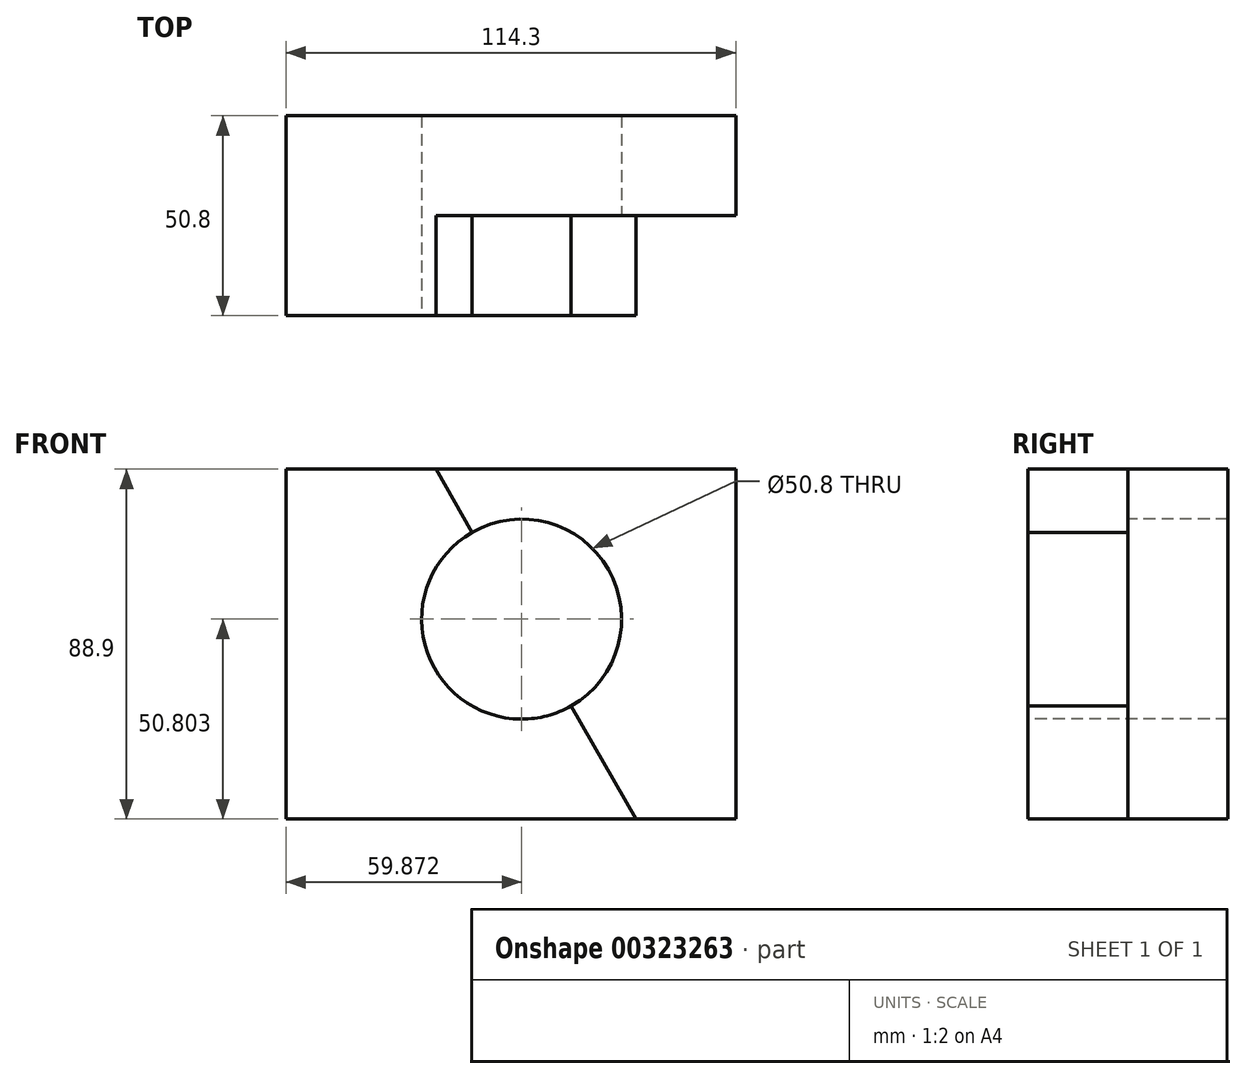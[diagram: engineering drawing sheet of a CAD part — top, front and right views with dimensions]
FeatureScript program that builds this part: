
annotation { "Feature Type Name" : "Feature", "Feature Type Description" : "" }
export const myFeature = defineFeature(function(context is Context, id is Id, definition is map)
    precondition{}
    {
        {
            var Q0;
            Q0=qCreatedBy(makeId("Front.planeOp"),FACE);
            var sketch = newSketch(context, id + "F0", { "sketchPlane" : qUnion([Q0])});
            skLineSegment(sketch, "E0", {"start": v(-45.19, -36.99) * mm, "end": v(69.11, -36.99) * mm});
            skLineSegment(sketch, "E1", {"start": v(69.11, -36.99) * mm, "end": v(69.11, 51.91) * mm});
            skLineSegment(sketch, "E2", {"start": v(69.11, 51.91) * mm, "end": v(-45.19, 51.91) * mm});
            skLineSegment(sketch, "E3", {"start": v(-45.19, 51.91) * mm, "end": v(-45.19, -36.99) * mm});
            skSolve(sketch);
        }
        {
            var Q0;
            Q0 = qSketchRegion(id + "F0", true);
            var Q1;
            Q1=makeQuery(id+"F0.imprint","IMPRINT",FACE,{"disambiguationData":[TD([[makeQuery(id+"F0.imprint","IMPRINT",EDGE,{"derivedFrom":sQuery(id+"F0.wireOp",EDGE,"E0")}),1.0]])]});
            extrude(context, id + "F1", {"entities" : qUnion([Q0, Q1]), "depth" : 25.4 * mm});
        }
        {
            var Q0;
            Q0=makeQuery(id+"F1.opExtrude","CAP_FACE",FACE,{"disambiguationData":[OSD([sQuery(id+"F0.wireOp",EDGE,"E0"),sQuery(id+"F0.wireOp",EDGE,"E1"),sQuery(id+"F0.wireOp",EDGE,"E2"),sQuery(id+"F0.wireOp",EDGE,"E3")])],"isStart":false});
            var sketch = newSketch(context, id + "F2", { "sketchPlane" : qUnion([Q0])});
            skLineSegment(sketch, "E4", {"start": v(-45.19, -36.99) * mm, "end": v(43.71, -36.99) * mm});
            skLineSegment(sketch, "E5", {"start": v(-45.19, -36.99) * mm, "end": v(-45.19, 51.91) * mm});
            skLineSegment(sketch, "E6", {"start": v(-45.19, 51.91) * mm, "end": v(-7.09, 51.91) * mm});
            skLineSegment(sketch, "E7", {"start": v(-7.09, 51.91) * mm, "end": v(43.71, -36.99) * mm});
            skSolve(sketch);
        }
        {
            var Q0;
            Q0=makeQuery(id+"F2.imprint","IMPRINT",FACE,{"disambiguationData":[TD([[makeQuery(id+"F2.imprint","IMPRINT",EDGE,{"derivedFrom":sQuery(id+"F2.wireOp",EDGE,"E4")}),1.0]])]});
            extrude(context, id + "F3", {"entities" : qUnion([Q0]), "operationType" : NewBodyOperationType.ADD, "depth" : 25.4 * mm});
        }
        {
            var Q0;
            Q0=makeQuery(id+"F3.opExtrude","CAP_FACE",FACE,{"disambiguationData":[OSD([sQuery(id+"F2.wireOp",EDGE,"E4"),sQuery(id+"F2.wireOp",EDGE,"E5"),sQuery(id+"F2.wireOp",EDGE,"E6"),sQuery(id+"F2.wireOp",EDGE,"E7")])],"isStart":false});
            var sketch = newSketch(context, id + "F4", { "sketchPlane" : qUnion([Q0])});
            skCircle(sketch, "E8", {"center": v(14.68, 13.81) * mm, "radius": 25.4 * mm});
            skSolve(sketch);
        }
        {
            var Q0;
            {var subQ0=sQuery(id+"F4.wireOp",EDGE,"E8");var subQ1=makeQuery(id+"F3.opExtrude","CAP_EDGE",EDGE,{"disambiguationData":[OSD([sQuery(id+"F2.wireOp",EDGE,"E7")])],"isStart":false});var subQ2=makeQuery(id+"F4.imprint","INTERSECT",VERTEX,{"disambiguationData":[OD(0.0)],"derivedFrom":[subQ1,subQ0]});Q0=makeQuery(id+"F4.imprint","IMPRINT",FACE,{"disambiguationData":[TD([[makeQuery(id+"F4.imprint","IMPRINT",EDGE,{"disambiguationData":[TD([[subQ2,1.0]])],"derivedFrom":subQ0}),1.0]])]});}
            var Q1;
            {var subQ0=sQuery(id+"F4.wireOp",EDGE,"E8");var subQ1=makeQuery(id+"F3.opExtrude","CAP_EDGE",EDGE,{"disambiguationData":[OSD([sQuery(id+"F2.wireOp",EDGE,"E7")])],"isStart":false});var subQ2=makeQuery(id+"F4.imprint","INTERSECT",VERTEX,{"disambiguationData":[OD(0.0)],"derivedFrom":[subQ1,subQ0]});Q1=makeQuery(id+"F4.imprint","IMPRINT",FACE,{"disambiguationData":[TD([[makeQuery(id+"F4.imprint","IMPRINT",EDGE,{"disambiguationData":[TD([[subQ2,-1.0]])],"derivedFrom":subQ0}),1.0]])]});}
            extrude(context, id + "F5", {"entities" : qUnion([Q0, Q1]), "operationType" : NewBodyOperationType.REMOVE, "oppositeDirection" : true, "depth" : 50.8 * mm});
        }
    });
